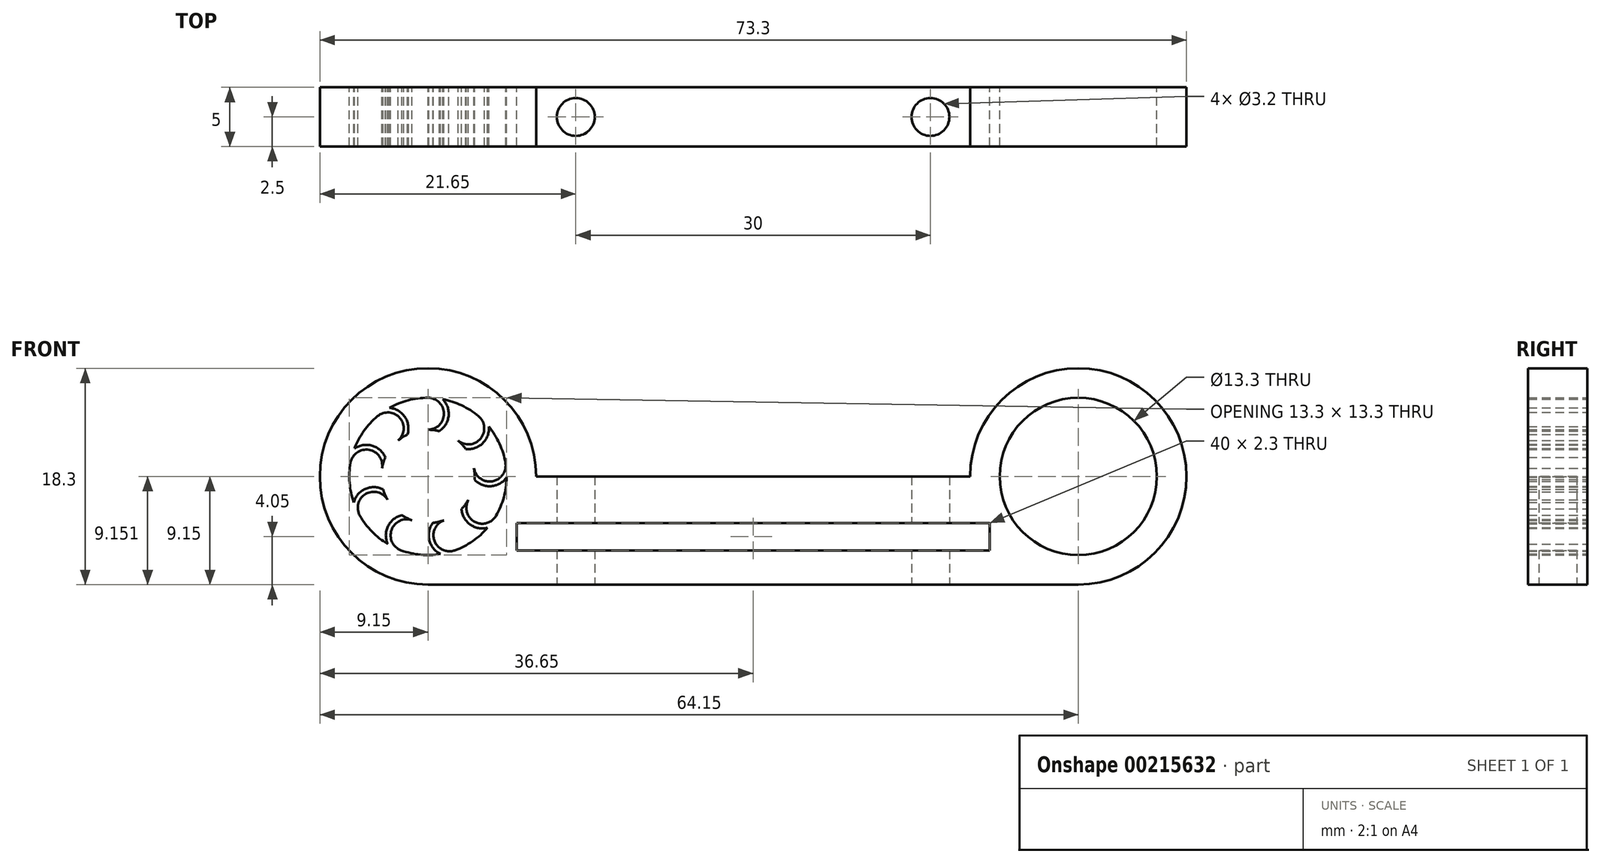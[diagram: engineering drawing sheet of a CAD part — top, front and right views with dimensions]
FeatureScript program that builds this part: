
annotation { "Feature Type Name" : "Feature", "Feature Type Description" : "" }
export const myFeature = defineFeature(function(context is Context, id is Id, definition is map)
    precondition{}
    {
        {
            var Q0;
            Q0=qCreatedBy(makeId("Front.planeOp"),FACE);
            var sketch = newSketch(context, id + "F0", { "sketchPlane" : qUnion([Q0])});
            skLineSegment(sketch, "E0", {"start": v(-27.5, -8.95) * mm, "end": v(0, -8.95) * mm, "construction": true});
            skLineSegment(sketch, "E1", {"start": v(0, -8.95) * mm, "end": v(27.5, -8.95) * mm, "construction": true});
            skCircle(sketch, "E2", {"center": v(-27.5, -8.95) * mm, "radius": 3.98 * mm});
            skCircle(sketch, "E3", {"center": v(27.5, -8.95) * mm, "radius": 3.98 * mm, "construction": true});
            skCircle(sketch, "E4", {"center": v(-27.5, -8.95) * mm, "radius": 6.65 * mm});
            skCircle(sketch, "E5", {"center": v(27.5, -8.95) * mm, "radius": 6.65 * mm});
            skCircle(sketch, "E6", {"center": v(-27.5, -8.95) * mm, "radius": 9.15 * mm});
            skCircle(sketch, "E7", {"center": v(27.5, -8.95) * mm, "radius": 9.15 * mm});
            skLineSegment(sketch, "E8", {"start": v(-27.5, -4.98) * mm, "end": v(-27.5, -2.3) * mm, "construction": true});
            skLineSegment(sketch, "E9.bottom", {"start": v(-27.5, -15.1) * mm, "end": v(27.5, -15.1) * mm});
            skLineSegment(sketch, "E9.top", {"start": v(-27.5, -18.1) * mm, "end": v(27.5, -18.1) * mm});
            skLineSegment(sketch, "E9.left", {"start": v(-27.5, -15.1) * mm, "end": v(-27.5, -18.1) * mm});
            skLineSegment(sketch, "E9.right", {"start": v(27.5, -15.1) * mm, "end": v(27.5, -18.1) * mm});
            skPoint(sketch, "E10", {"position": v(0, -15.1) * mm});
            skLineSegment(sketch, "E11.bottom", {"start": v(20.85, -8.95) * mm, "end": v(-20.85, -8.95) * mm});
            skLineSegment(sketch, "E11.top", {"start": v(20.85, -15.1) * mm, "end": v(-20.85, -15.1) * mm});
            skLineSegment(sketch, "E11.left", {"start": v(20.85, -8.95) * mm, "end": v(20.85, -15.1) * mm});
            skLineSegment(sketch, "E11.right", {"start": v(-20.85, -8.95) * mm, "end": v(-20.85, -15.1) * mm});
            skSolve(sketch);
        }
        {
            var Q0;
            Q0=qSketchRegion(id+"F0",true);
            var Q1;
            {var subQ3=sQuery(id+"F0.wireOp",EDGE,"E11.right");Q1=makeQuery(id+"F0.imprint","IMPRINT",FACE,{"disambiguationData":[TD([[makeQuery(id+"F0.imprint","IMPRINT",EDGE,{"derivedFrom":subQ3}),-1.0]])]});}
            var Q2;
            {var subQ3=sQuery(id+"F0.wireOp",EDGE,"E11.left");Q2=makeQuery(id+"F0.imprint","IMPRINT",FACE,{"disambiguationData":[TD([[makeQuery(id+"F0.imprint","IMPRINT",EDGE,{"derivedFrom":subQ3}),1.0]])]});}
            extrude(context, id + "F1", {"entities" : qUnion([Q0, Q1, Q2]), "depth" : 5 * mm});
        }
        {
            var Q0;
            Q0=makeQuery(id+"F1.opExtrude","CAP_FACE",FACE,{"disambiguationData":[OSD([sQuery(id+"F0.wireOp",EDGE,"E4"),sQuery(id+"F0.wireOp",EDGE,"E5"),sQuery(id+"F0.wireOp",EDGE,"E6"),sQuery(id+"F0.wireOp",EDGE,"E7"),sQuery(id+"F0.wireOp",EDGE,"E9.bottom"),sQuery(id+"F0.wireOp",EDGE,"E9.top"),sQuery(id+"F0.wireOp",EDGE,"E9.left"),sQuery(id+"F0.wireOp",EDGE,"E9.right")])],"isStart":true});
            var sketch = newSketch(context, id + "F2", { "sketchPlane" : qUnion([Q0])});
            skCircle(sketch, "E12.0", {"center": v(27.5, -8.95) * mm, "radius": 6.65 * mm});
            skCircle(sketch, "E13", {"center": v(27.5, -8.95) * mm, "radius": 3.95 * mm});
            skLineSegment(sketch, "E14", {"start": v(27.5, -8.95) * mm, "end": v(27.5, -2.3) * mm, "construction": true});
            skArc(sketch, "E15", {"start": v(27.5, -2.3) * mm, "mid": v(26.15, -3.65) * mm, "end": v(27.5, -5) * mm});
            skArc(sketch, "E16", {"start": v(27.5, -1.9) * mm, "mid": v(25.82, -3.15) * mm, "end": v(26.55, -5.12) * mm});
            skArc(sketch, "E17.1.0", {"start": v(22.97, -3.55) * mm, "mid": v(22.49, -5.59) * mm, "end": v(24.3, -6.63) * mm});
            skArc(sketch, "E17.1.1", {"start": v(23.23, -3.86) * mm, "mid": v(23.06, -5.76) * mm, "end": v(24.96, -5.92) * mm});
            skArc(sketch, "E17.2.0", {"start": v(20.56, -7.73) * mm, "mid": v(21.5, -9.6) * mm, "end": v(23.56, -9.22) * mm});
            skArc(sketch, "E17.2.1", {"start": v(20.95, -7.8) * mm, "mid": v(22.05, -9.36) * mm, "end": v(23.61, -8.26) * mm});
            skArc(sketch, "E17.3.0", {"start": v(21.4, -12.48) * mm, "mid": v(23.32, -13.3) * mm, "end": v(24.66, -11.7) * mm});
            skArc(sketch, "E17.3.1", {"start": v(21.74, -12.28) * mm, "mid": v(23.59, -12.77) * mm, "end": v(24.08, -10.93) * mm});
            skArc(sketch, "E17.4.0", {"start": v(25.09, -15.58) * mm, "mid": v(27.1, -14.97) * mm, "end": v(27.09, -12.88) * mm});
            skArc(sketch, "E17.4.1", {"start": v(25.23, -15.2) * mm, "mid": v(26.96, -14.4) * mm, "end": v(26.15, -12.66) * mm});
            skArc(sketch, "E17.5.0", {"start": v(29.91, -15.58) * mm, "mid": v(31.06, -13.82) * mm, "end": v(29.7, -12.23) * mm});
            skArc(sketch, "E17.5.1", {"start": v(29.77, -15.2) * mm, "mid": v(30.58, -13.47) * mm, "end": v(28.85, -12.66) * mm});
            skArc(sketch, "E17.6.0", {"start": v(33.6, -12.48) * mm, "mid": v(33.36, -10.4) * mm, "end": v(31.3, -10.04) * mm});
            skArc(sketch, "E17.6.1", {"start": v(33.26, -12.28) * mm, "mid": v(32.76, -10.43) * mm, "end": v(30.92, -10.93) * mm});
            skArc(sketch, "E17.7.0", {"start": v(34.44, -7.73) * mm, "mid": v(32.92, -6.3) * mm, "end": v(31.1, -7.34) * mm});
            skArc(sketch, "E17.7.1", {"start": v(34.05, -7.8) * mm, "mid": v(32.49, -6.7) * mm, "end": v(31.39, -8.26) * mm});
            skArc(sketch, "E17.8.0", {"start": v(32.03, -3.55) * mm, "mid": v(29.94, -3.43) * mm, "end": v(29.23, -5.4) * mm});
            skArc(sketch, "E17.8.1", {"start": v(31.77, -3.86) * mm, "mid": v(29.87, -4.02) * mm, "end": v(30.04, -5.92) * mm});
            skSolve(sketch);
        }
        {
            var Q0;
            {var subQ0=sQuery(id+"F2.wireOp",EDGE,"E15");Q0=makeQuery(id+"F2.imprint","IMPRINT",FACE,{"disambiguationData":[TD([[makeQuery(id+"F2.imprint","IMPRINT",EDGE,{"derivedFrom":subQ0}),-1.0]])]});}
            var Q1;
            {var subQ0=sQuery(id+"F2.wireOp",EDGE,"E17.1.1");Q1=makeQuery(id+"F2.imprint","IMPRINT",FACE,{"disambiguationData":[TD([[makeQuery(id+"F2.imprint","IMPRINT",EDGE,{"derivedFrom":subQ0}),-1.0]])]});}
            var Q2;
            {var subQ0=sQuery(id+"F2.wireOp",EDGE,"E17.2.1");Q2=makeQuery(id+"F2.imprint","IMPRINT",FACE,{"disambiguationData":[TD([[makeQuery(id+"F2.imprint","IMPRINT",EDGE,{"derivedFrom":subQ0}),-1.0]])]});}
            var Q3;
            {var subQ0=sQuery(id+"F2.wireOp",EDGE,"E17.3.1");Q3=makeQuery(id+"F2.imprint","IMPRINT",FACE,{"disambiguationData":[TD([[makeQuery(id+"F2.imprint","IMPRINT",EDGE,{"derivedFrom":subQ0}),-1.0]])]});}
            var Q4;
            {var subQ0=sQuery(id+"F2.wireOp",EDGE,"E17.4.1");Q4=makeQuery(id+"F2.imprint","IMPRINT",FACE,{"disambiguationData":[TD([[makeQuery(id+"F2.imprint","IMPRINT",EDGE,{"derivedFrom":subQ0}),-1.0]])]});}
            var Q5;
            {var subQ0=sQuery(id+"F2.wireOp",EDGE,"E17.5.1");Q5=makeQuery(id+"F2.imprint","IMPRINT",FACE,{"disambiguationData":[TD([[makeQuery(id+"F2.imprint","IMPRINT",EDGE,{"derivedFrom":subQ0}),-1.0]])]});}
            var Q6;
            {var subQ0=sQuery(id+"F2.wireOp",EDGE,"E17.6.1");Q6=makeQuery(id+"F2.imprint","IMPRINT",FACE,{"disambiguationData":[TD([[makeQuery(id+"F2.imprint","IMPRINT",EDGE,{"derivedFrom":subQ0}),-1.0]])]});}
            var Q7;
            {var subQ0=sQuery(id+"F2.wireOp",EDGE,"E17.7.1");Q7=makeQuery(id+"F2.imprint","IMPRINT",FACE,{"disambiguationData":[TD([[makeQuery(id+"F2.imprint","IMPRINT",EDGE,{"derivedFrom":subQ0}),-1.0]])]});}
            var Q8;
            {var subQ0=sQuery(id+"F2.wireOp",EDGE,"E17.8.1");Q8=makeQuery(id+"F2.imprint","IMPRINT",FACE,{"disambiguationData":[TD([[makeQuery(id+"F2.imprint","IMPRINT",EDGE,{"derivedFrom":subQ0}),-1.0]])]});}
            var Q9;
            Q9=makeQuery(id+"F1.opExtrude","CAP_FACE",FACE,{"disambiguationData":[OSD([sQuery(id+"F0.wireOp",EDGE,"E4"),sQuery(id+"F0.wireOp",EDGE,"E5"),sQuery(id+"F0.wireOp",EDGE,"E6"),sQuery(id+"F0.wireOp",EDGE,"E7"),sQuery(id+"F0.wireOp",EDGE,"E9.bottom"),sQuery(id+"F0.wireOp",EDGE,"E9.top"),sQuery(id+"F0.wireOp",EDGE,"E9.left"),sQuery(id+"F0.wireOp",EDGE,"E9.right")])],"isStart":false});
            extrude(context, id + "F3", {"entities" : qUnion([Q0, Q1, Q2, Q3, Q4, Q5, Q6, Q7, Q8]), "operationType" : NewBodyOperationType.ADD, "endBound" : BoundingType.UP_TO_SURFACE, "oppositeDirection" : true, "endBoundEntityFace" : qUnion([Q9]), "depth" : 25 * mm});
        }
        {
            var Q0;
            Q0=qCreatedBy(makeId("Right.planeOp"),FACE);
            var sketch = newSketch(context, id + "F4", { "sketchPlane" : qUnion([Q0])});
            skLineSegment(sketch, "E18.0", {"start": v(-5, -18.1) * mm, "end": v(-5, 0.2) * mm});
            skLineSegment(sketch, "E19.0", {"start": v(-5, -18.1) * mm, "end": v(0, -18.1) * mm});
            skLineSegment(sketch, "E20.0", {"start": v(-5, -8.95) * mm, "end": v(0, -8.95) * mm});
            skLineSegment(sketch, "E21.bottom", {"start": v(-5, -12.9) * mm, "end": v(0, -12.9) * mm});
            skLineSegment(sketch, "E21.top", {"start": v(-5, -15.2) * mm, "end": v(0, -15.2) * mm});
            skLineSegment(sketch, "E21.left", {"start": v(-5, -12.9) * mm, "end": v(-5, -15.2) * mm});
            skLineSegment(sketch, "E21.right", {"start": v(0, -12.9) * mm, "end": v(0, -15.2) * mm});
            skSolve(sketch);
        }
        {
            var Q0;
            Q0 = qSketchRegion(id + "F4", true);
            extrude(context, id + "F5", {"entities" : qUnion([Q0]), "operationType" : NewBodyOperationType.REMOVE, "endBound" : BoundingType.SYMMETRIC, "oppositeDirection" : true, "depth" : 40 * mm});
        }
        {
            var Q0;
            Q0=makeQuery(id+"F1.opExtrude","SWEPT_FACE",FACE,{"disambiguationData":[OSD([sQuery(id+"F0.wireOp",EDGE,"E9.top")])]});
            var sketch = newSketch(context, id + "F6", { "sketchPlane" : qUnion([Q0])});
            skCircle(sketch, "E22", {"center": v(-15, 2.5) * mm, "radius": 1.6 * mm});
            skPoint(sketch, "E22.centerSnap0", {"position": v(-27.5, 2.5) * mm});
            skCircle(sketch, "E23", {"center": v(15, 2.5) * mm, "radius": 1.6 * mm});
            skPoint(sketch, "E23.centerSnap0", {"position": v(27.5, 2.5) * mm});
            skSolve(sketch);
        }
        {
            var Q0;
            Q0 = qSketchRegion(id + "F6", true);
            extrude(context, id + "F7", {"entities" : qUnion([Q0]), "operationType" : NewBodyOperationType.REMOVE, "endBound" : BoundingType.THROUGH_ALL, "oppositeDirection" : true, "depth" : 25 * mm});
        }
    });
